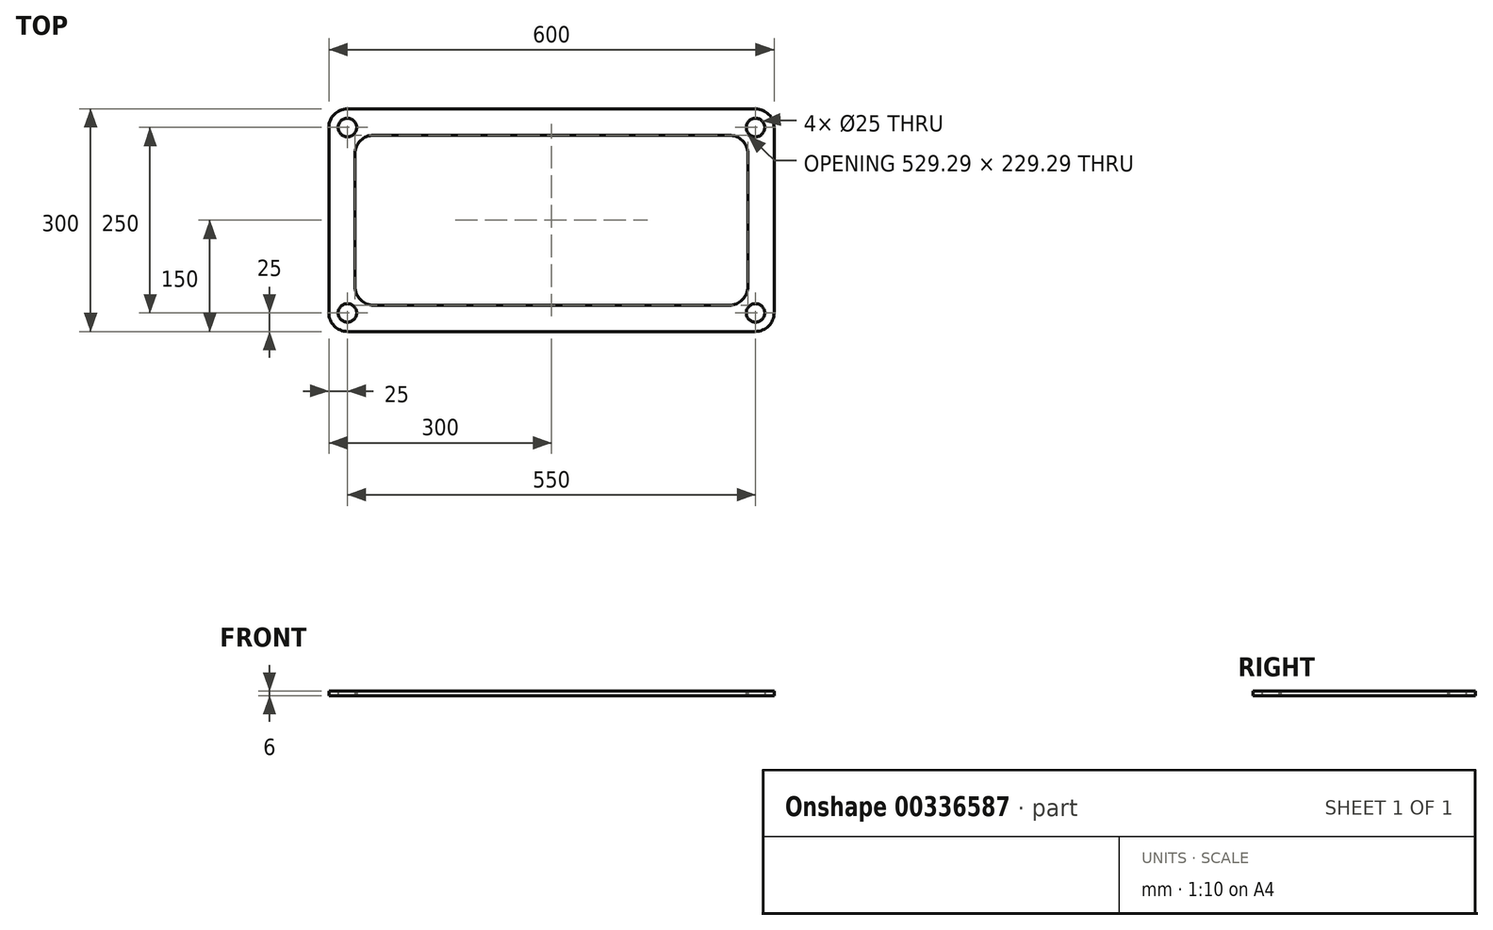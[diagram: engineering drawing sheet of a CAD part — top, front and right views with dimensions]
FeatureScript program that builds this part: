
annotation { "Feature Type Name" : "Feature", "Feature Type Description" : "" }
export const myFeature = defineFeature(function(context is Context, id is Id, definition is map)
    precondition{}
    {
        {
            var Q0;
            Q0=qCreatedBy(makeId("Top.planeOp"),FACE);
            var sketch = newSketch(context, id + "F0", { "sketchPlane" : qUnion([Q0])});
            skLineSegment(sketch, "E0.bottom", {"start": v(275, -150) * mm, "end": v(-275, -150) * mm});
            skLineSegment(sketch, "E0.top", {"start": v(275, 150) * mm, "end": v(-275, 150) * mm});
            skLineSegment(sketch, "E0.left", {"start": v(300, -125) * mm, "end": v(300, 125) * mm});
            skLineSegment(sketch, "E0.right", {"start": v(-300, -125) * mm, "end": v(-300, 125) * mm});
            skPoint(sketch, "E0.middle", {"position": v(0, 0) * mm});
            skPoint(sketch, "E1.visualSharp", {"position": v(-300, 150) * mm});
            skArc(sketch, "E1.filletArc", {"start": v(-275, 150) * mm, "mid": v(-292.68, 142.68) * mm, "end": v(-300, 125) * mm});
            skPoint(sketch, "E2.visualSharp", {"position": v(-300, -150) * mm});
            skArc(sketch, "E2.filletArc", {"start": v(-300, -125) * mm, "mid": v(-292.68, -142.68) * mm, "end": v(-275, -150) * mm});
            skPoint(sketch, "E3.visualSharp", {"position": v(300, 150) * mm});
            skArc(sketch, "E3.filletArc", {"start": v(300, 125) * mm, "mid": v(292.68, 142.68) * mm, "end": v(275, 150) * mm});
            skPoint(sketch, "E4.visualSharp", {"position": v(300, -150) * mm});
            skArc(sketch, "E4.filletArc", {"start": v(275, -150) * mm, "mid": v(292.68, -142.68) * mm, "end": v(300, -125) * mm});
            skLineSegment(sketch, "E5.0", {"start": v(239.64, -114.64) * mm, "end": v(-239.64, -114.64) * mm});
            skLineSegment(sketch, "E5.1", {"start": v(264.64, -89.64) * mm, "end": v(264.64, 89.64) * mm});
            skLineSegment(sketch, "E5.2", {"start": v(239.64, 114.64) * mm, "end": v(-239.64, 114.64) * mm});
            skLineSegment(sketch, "E5.3", {"start": v(-264.64, -89.64) * mm, "end": v(-264.64, 89.64) * mm});
            skPoint(sketch, "E6.visualSharp", {"position": v(-264.64, 114.64) * mm});
            skArc(sketch, "E6.filletArc", {"start": v(-239.64, 114.64) * mm, "mid": v(-257.32, 107.32) * mm, "end": v(-264.64, 89.64) * mm});
            skPoint(sketch, "E7.visualSharp", {"position": v(-264.64, -114.64) * mm});
            skArc(sketch, "E7.filletArc", {"start": v(-264.64, -89.64) * mm, "mid": v(-257.32, -107.32) * mm, "end": v(-239.64, -114.64) * mm});
            skPoint(sketch, "E8.visualSharp", {"position": v(264.64, 114.64) * mm});
            skArc(sketch, "E8.filletArc", {"start": v(264.64, 89.64) * mm, "mid": v(257.32, 107.32) * mm, "end": v(239.64, 114.64) * mm});
            skPoint(sketch, "E9.visualSharp", {"position": v(264.64, -114.64) * mm});
            skArc(sketch, "E9.filletArc", {"start": v(239.64, -114.64) * mm, "mid": v(257.32, -107.32) * mm, "end": v(264.64, -89.64) * mm});
            skSolve(sketch);
        }
        {
            var Q0;
            Q0=makeQuery(id+"F0.imprint","IMPRINT",FACE,{"disambiguationData":[TD([[makeQuery(id+"F0.imprint","IMPRINT",EDGE,{"derivedFrom":sQuery(id+"F0.wireOp",EDGE,"E0.bottom")}),-1.0]])]});
            extrude(context, id + "F1", {"entities" : qUnion([Q0]), "depth" : 6 * mm});
        }
        {
            var Q0;
            Q0=sQuery(id+"F0.wireOp",VERTEX,"E2.filletArc.center");
            var Q1;
            Q1=makeQuery(id+"F1.opExtrude","SWEPT_BODY",BODY,{"disambiguationData":[OSD([sQuery(id+"F0.wireOp",EDGE,"E0.bottom"),sQuery(id+"F0.wireOp",EDGE,"E0.top"),sQuery(id+"F0.wireOp",EDGE,"E0.left"),sQuery(id+"F0.wireOp",EDGE,"E0.right"),sQuery(id+"F0.wireOp",EDGE,"E1.filletArc"),sQuery(id+"F0.wireOp",EDGE,"E2.filletArc"),sQuery(id+"F0.wireOp",EDGE,"E3.filletArc"),sQuery(id+"F0.wireOp",EDGE,"E4.filletArc")])]});
            hole(context, id + "F2", {"style" : HoleStyle.SIMPLE, "endStyle" : HoleEndStyle.THROUGH, "oppositeDirection" : true, "holeDiameter" : 25 * mm, "tappedDepth" : 12 * mm, "tapClearance" : 3, "locations" : qUnion([Q0]), "scope" : qUnion([Q1])});
        }
        {
            var Q0;
            Q0=sQuery(id+"F0.wireOp",VERTEX,"E1.filletArc.center");
            var Q1;
            Q1=sQuery(id+"F0.wireOp",VERTEX,"E4.filletArc.center");
            var Q2;
            Q2=makeQuery(id+"F1.opExtrude","SWEPT_BODY",BODY,{"disambiguationData":[OSD([sQuery(id+"F0.wireOp",EDGE,"E0.bottom"),sQuery(id+"F0.wireOp",EDGE,"E0.top"),sQuery(id+"F0.wireOp",EDGE,"E0.left"),sQuery(id+"F0.wireOp",EDGE,"E0.right"),sQuery(id+"F0.wireOp",EDGE,"E1.filletArc"),sQuery(id+"F0.wireOp",EDGE,"E2.filletArc"),sQuery(id+"F0.wireOp",EDGE,"E3.filletArc"),sQuery(id+"F0.wireOp",EDGE,"E4.filletArc")])]});
            hole(context, id + "F3", {"style" : HoleStyle.SIMPLE, "endStyle" : HoleEndStyle.THROUGH, "oppositeDirection" : true, "holeDiameter" : 25 * mm, "tappedDepth" : 12 * mm, "tapClearance" : 3, "locations" : qUnion([Q0, Q1]), "scope" : qUnion([Q2])});
        }
        {
            var Q0;
            Q0=sQuery(id+"F0.wireOp",VERTEX,"E3.filletArc.center");
            var Q1;
            Q1=makeQuery(id+"F1.opExtrude","SWEPT_BODY",BODY,{"disambiguationData":[OSD([sQuery(id+"F0.wireOp",EDGE,"E0.bottom"),sQuery(id+"F0.wireOp",EDGE,"E0.top"),sQuery(id+"F0.wireOp",EDGE,"E0.left"),sQuery(id+"F0.wireOp",EDGE,"E0.right"),sQuery(id+"F0.wireOp",EDGE,"E1.filletArc"),sQuery(id+"F0.wireOp",EDGE,"E2.filletArc"),sQuery(id+"F0.wireOp",EDGE,"E3.filletArc"),sQuery(id+"F0.wireOp",EDGE,"E4.filletArc")])]});
            hole(context, id + "F4", {"style" : HoleStyle.SIMPLE, "endStyle" : HoleEndStyle.THROUGH, "oppositeDirection" : true, "holeDiameter" : 25 * mm, "tappedDepth" : 12 * mm, "tapClearance" : 3, "locations" : qUnion([Q0]), "scope" : qUnion([Q1])});
        }
    });
